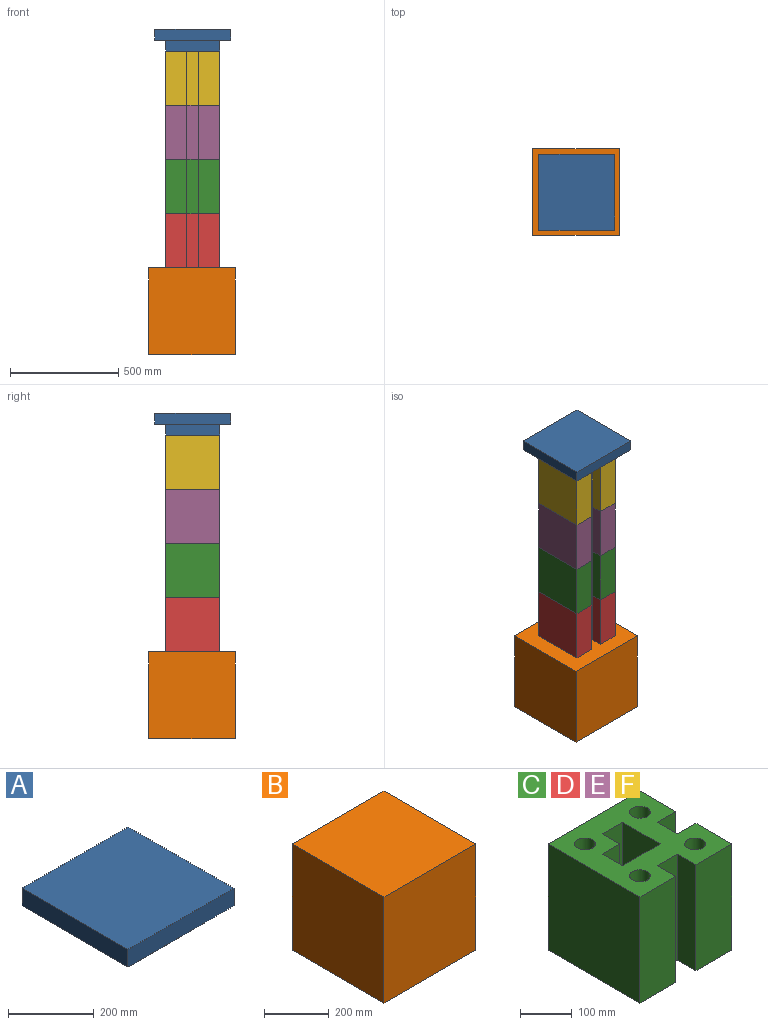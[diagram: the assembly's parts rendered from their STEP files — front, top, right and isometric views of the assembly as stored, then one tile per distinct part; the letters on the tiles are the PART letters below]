
ASSEMBLY  parts=6 mates=5
PART A: 11 faces, bbox 350x350x100 mm
  f0: plane 350x50mm, normal (0,-1,0), area 17500mm2, adj f1,f3,f4,f5
  f1: plane 350x50mm, normal (1,0,0), area 17500mm2, adj f0,f2,f4,f5
  f2: plane 350x50mm, normal (0,1,0), area 17500mm2, adj f1,f3,f4,f5
  f3: plane 350x50mm, normal (-1,0,0), area 17500mm2, adj f0,f2,f4,f5
  f4: plane 350x350mm, normal (0,0,1), area 122500mm2, adj f0,f1,f2,f3
  f5: plane 350x350mm, normal (0,0,-1), area 60000mm2, adj f0,f1,f2,f3,f6,f7,f8,f9
  f6: plane 250x50mm, normal (1,0,0), area 12500mm2, adj f5,f7,f9,f10
  f7: plane 250x50mm, normal (0,1,0), area 12500mm2, adj f5,f6,f8,f10
  f8: plane 250x50mm, normal (-1,0,0), area 12500mm2, adj f5,f7,f9,f10
  f9: plane 250x50mm, normal (0,-1,0), area 12500mm2, adj f5,f6,f8,f10
  f10: plane 250x250mm, normal (0,0,-1), area 62500mm2, adj f6,f7,f8,f9
PART B: 6 faces, bbox 400x400x400 mm
  f0: plane 400x400mm, normal (0,-1,0), area 160000mm2, adj f1,f3,f4,f5
  f1: plane 400x400mm, normal (1,0,0), area 160000mm2, adj f0,f2,f4,f5
  f2: plane 400x400mm, normal (0,1,0), area 160000mm2, adj f1,f3,f4,f5
  f3: plane 400x400mm, normal (-1,0,0), area 160000mm2, adj f0,f2,f4,f5
  f4: plane 400x400mm, normal (0,0,1), area 160000mm2, adj f0,f1,f2,f3
  f5: plane 400x400mm, normal (0,0,-1), area 160000mm2, adj f0,f1,f2,f3
PART C: 24 faces, bbox 250x250x250 mm
  f0: plane 250x55mm, normal (0,-1,0), area 13750mm2, adj f1,f21,f22,f23
  f1: plane 250x102.5mm, normal (-1,0,0), area 25625mm2, adj f0,f2,f22,f23
  f2: plane 250x102.5mm, normal (0,1,0), area 25625mm2, adj f1,f3,f22,f23
  f3: plane 250x55mm, normal (1,0,0), area 13750mm2, adj f2,f4,f22,f23
  f4: plane 250x47.5mm, normal (0,-1,0), area 11875mm2, adj f3,f21,f22,f23
  f5: plane 250x250mm, normal (-1,0,0), area 62500mm2, adj f6,f16,f22,f23
  f6: plane 250x97.5mm, normal (0,-1,0), area 24375mm2, adj f5,f7,f22,f23
  f7: plane 250x50mm, normal (1,0,0), area 12500mm2, adj f6,f8,f22,f23
  f8: plane 250x55mm, normal (0,-1,0), area 13750mm2, adj f7,f9,f22,f23
  f9: plane 250x50mm, normal (-1,0,0), area 12500mm2, adj f8,f10,f22,f23
  f10: plane 250x97.5mm, normal (0,-1,0), area 24375mm2, adj f9,f11,f22,f23
  f11: plane 250x97.5mm, normal (1,0,0), area 24375mm2, adj f10,f12,f22,f23
  f12: plane 250x50mm, normal (0,1,0), area 12500mm2, adj f11,f13,f22,f23
  f13: plane 250x55mm, normal (1,0,0), area 13750mm2, adj f12,f14,f22,f23
  f14: plane 250x50mm, normal (0,-1,0), area 12500mm2, adj f13,f15,f22,f23
  f15: plane 250x97.5mm, normal (1,0,0), area 24375mm2, adj f14,f16,f22,f23
  f16: plane 250x250mm, normal (0,1,0), area 62500mm2, adj f5,f15,f22,f23
  f17: cylinder r=20mm len=250mm, axis (0,0,-1), area 31415.9mm2, adj f22,f23
  f18: cylinder r=20mm len=250mm, axis (0,0,-1), area 31415.9mm2, adj f22,f23
  f19: cylinder r=20mm len=250mm, axis (0,0,-1), area 31415.9mm2, adj f22,f23
  f20: cylinder r=20mm len=250mm, axis (0,0,-1), area 31415.9mm2, adj f22,f23
  f21: plane 250x47.5mm, normal (1,0,0), area 11875mm2, adj f0,f4,f22,f23
  f22: plane 250x250mm, normal (0,0,1), area 43723.5mm2, adj f0,f1,f2,f3,f4,f5,f6,f7
  f23: plane 250x250mm, normal (0,0,-1), area 43723.5mm2, adj f0,f1,f2,f3,f4,f5,f6,f7
PART D: same geometry as C
PART E: same geometry as C
PART F: same geometry as C
PLACE A t=(66.89,-219.51,320.43)mm
PLACE B t=(63.67,-216.29,-929.57)mm fixed
PLACE C t=(66.89,-219.51,-354.57)mm
PLACE D t=(66.89,-219.51,-604.57)mm
PLACE E t=(66.89,-219.51,-104.57)mm
PLACE F t=(66.89,-219.51,145.43)mm
MATE fastened E.f23 <-> C.f22  axis (0,0,-1) through (-58.11,-94.51,-229.57)mm
MATE fastened C.f23 <-> D.f22  axis (0,0,-1) through (-58.11,-94.51,-479.57)mm
MATE fastened D.f23 <-> B.f4  axis (0,0,-1) through (63.67,-216.29,-729.57)mm
MATE fastened F.f23 <-> E.f22  axis (0,0,-1) through (-58.11,-94.51,20.43)mm
MATE fastened A.f10 <-> F.f22  axis (0,0,-1) through (191.89,-344.51,270.43)mm
